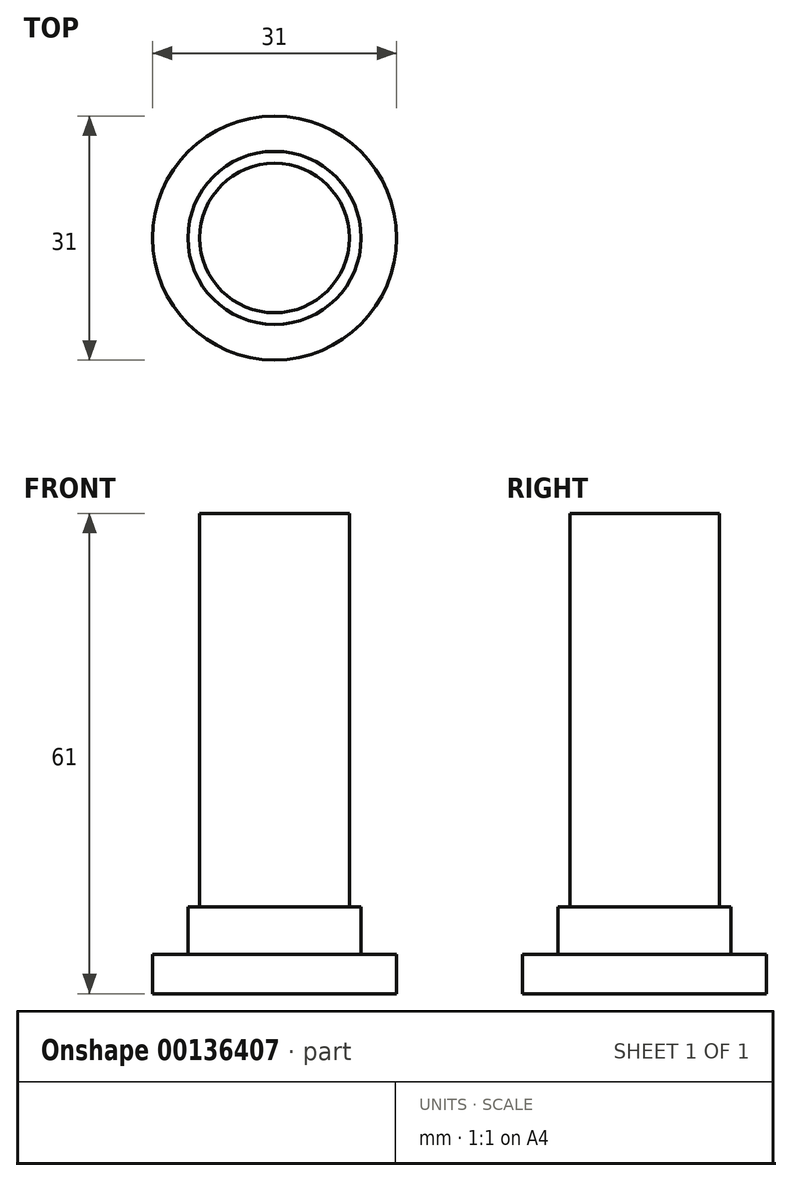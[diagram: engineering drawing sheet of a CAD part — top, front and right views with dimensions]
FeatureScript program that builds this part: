
annotation { "Feature Type Name" : "Feature", "Feature Type Description" : "" }
export const myFeature = defineFeature(function(context is Context, id is Id, definition is map)
    precondition{}
    {
        {
            var Q0;
            Q0=qCreatedBy(makeId("Front.planeOp"),FACE);
            var sketch = newSketch(context, id + "F0", { "sketchPlane" : qUnion([Q0])});
            skLineSegment(sketch, "E0.bottom", {"start": v(-9.46, 41) * mm, "end": v(0.04, 41) * mm});
            skLineSegment(sketch, "E0.top", {"start": v(-9.46, -20) * mm, "end": v(0.04, -20) * mm});
            skLineSegment(sketch, "E0.left", {"start": v(-9.46, 41) * mm, "end": v(-9.46, -9) * mm});
            skLineSegment(sketch, "E1.bottom", {"start": v(-15.46, -15) * mm, "end": v(-10.96, -15) * mm});
            skLineSegment(sketch, "E1.top", {"start": v(-15.46, -20) * mm, "end": v(0.04, -20) * mm});
            skLineSegment(sketch, "E1.left", {"start": v(-15.46, -15) * mm, "end": v(-15.46, -20) * mm});
            skLineSegment(sketch, "E2.top", {"start": v(-10.96, -9) * mm, "end": v(-9.46, -9) * mm});
            skLineSegment(sketch, "E2.left", {"start": v(-10.96, -15) * mm, "end": v(-10.96, -9) * mm});
            skLineSegment(sketch, "E3", {"start": v(0.04, 41) * mm, "end": v(0.04, -20) * mm});
            skPoint(sketch, "E4.orphan", {"position": v(9.54, 41) * mm});
            skPoint(sketch, "E1.right.end.orphan", {"position": v(15.54, -20) * mm});
            skPoint(sketch, "E5.orphan", {"position": v(9.54, -20) * mm});
            skSolve(sketch);
        }
        {
            var Q0;
            Q0 = qSketchRegion(id + "F0", true);
            var Q1;
            Q1=sQuery(id+"F0.wireOp",EDGE,"E3");
            revolve(context, id + "F1", {"entities" : qUnion([Q0]), "axis" : qUnion([Q1]), "revolveType" : RevolveType.FULL});
        }
    });
